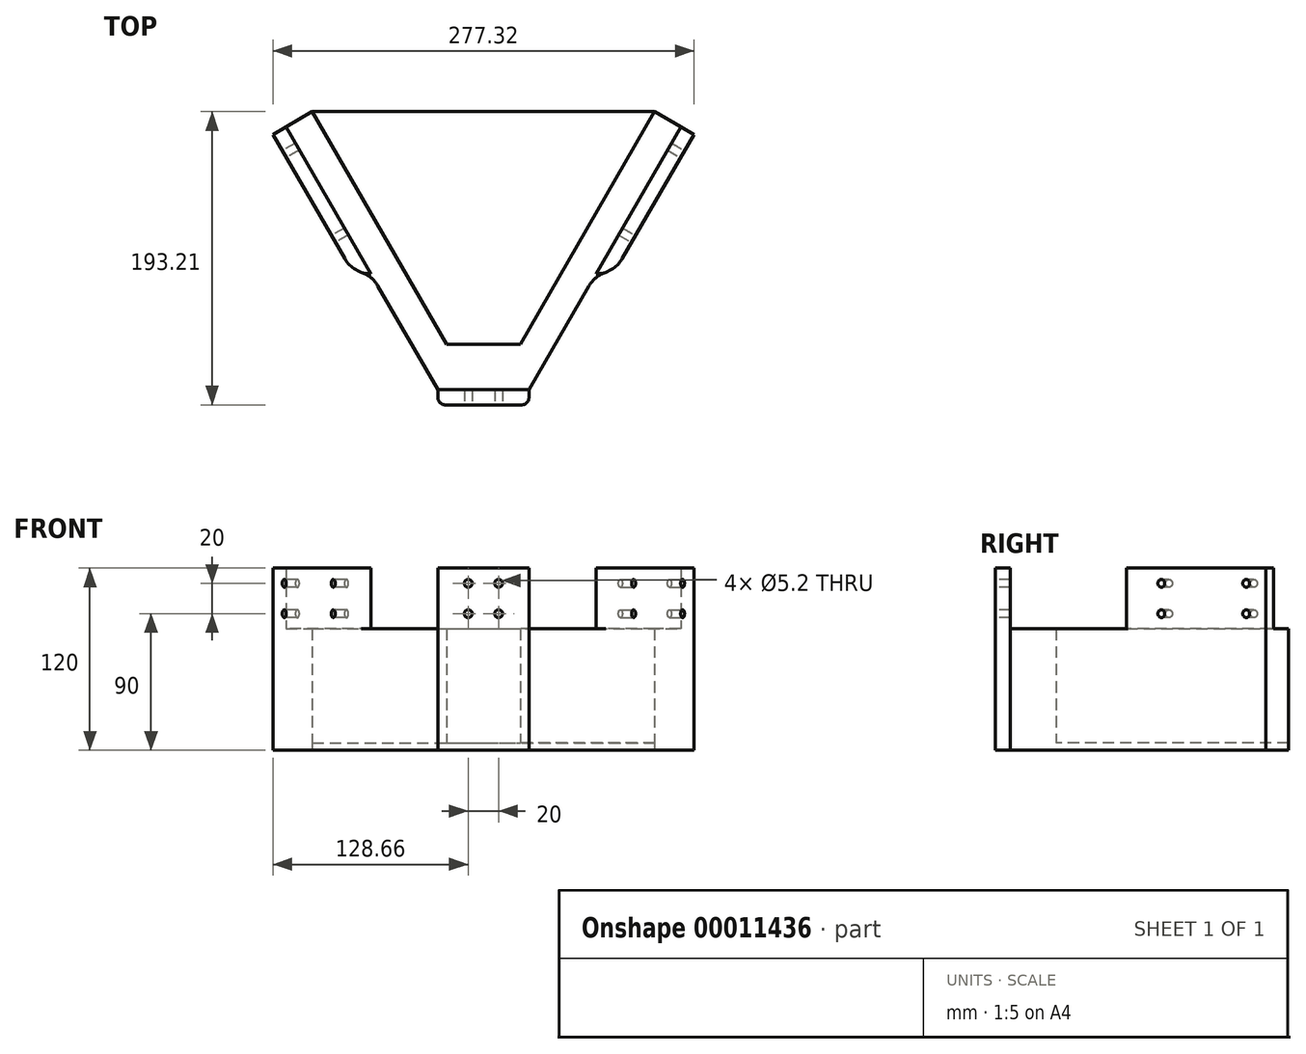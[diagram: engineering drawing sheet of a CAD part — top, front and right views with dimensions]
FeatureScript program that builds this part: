
annotation { "Feature Type Name" : "Feature", "Feature Type Description" : "" }
export const myFeature = defineFeature(function(context is Context, id is Id, definition is map)
    precondition{}
    {
        {
            var Q0;
            Q0=qCreatedBy(makeId("Top.planeOp"),FACE);
            var sketch = newSketch(context, id + "F0", { "sketchPlane" : qUnion([Q0])});
            skLineSegment(sketch, "E0.rect.bottom", {"start": v(-20, 20) * mm, "end": v(20, 20) * mm});
            skLineSegment(sketch, "E0.rect.top", {"start": v(-20, -20) * mm, "end": v(20, -20) * mm});
            skLineSegment(sketch, "E0.rect.left", {"start": v(-20, 20) * mm, "end": v(-20, -20) * mm});
            skLineSegment(sketch, "E0.rect.right", {"start": v(20, 20) * mm, "end": v(20, -20) * mm});
            skPoint(sketch, "E0.rect.middle", {"position": v(0, 0) * mm});
            skLineSegment(sketch, "E1.rect.bottom", {"start": v(-30, 30) * mm, "end": v(30, 30) * mm});
            skLineSegment(sketch, "E1.rect.top", {"start": v(-30, -30) * mm, "end": v(30, -30) * mm});
            skLineSegment(sketch, "E1.rect.left", {"start": v(-30, 30) * mm, "end": v(-30, -30) * mm});
            skLineSegment(sketch, "E1.rect.right", {"start": v(30, 30) * mm, "end": v(30, -30) * mm});
            skLineSegment(sketch, "E2", {"start": v(30, 30) * mm, "end": v(60, 81.96) * mm});
            skLineSegment(sketch, "E3", {"start": v(-30, 30) * mm, "end": v(-60, 81.96) * mm});
            skLineSegment(sketch, "E4", {"start": v(60, 81.96) * mm, "end": v(68.66, 76.96) * mm});
            skLineSegment(sketch, "E5", {"start": v(68.66, 76.96) * mm, "end": v(30, 10) * mm});
            skLineSegment(sketch, "E6", {"start": v(-60, 81.96) * mm, "end": v(-68.66, 76.96) * mm});
            skLineSegment(sketch, "E7", {"start": v(-68.66, 76.96) * mm, "end": v(-30, 10) * mm});
            skLineSegment(sketch, "E8", {"start": v(30, 30) * mm, "end": v(55.98, 15) * mm});
            skLineSegment(sketch, "E9", {"start": v(55.98, 15) * mm, "end": v(30, -30) * mm});
            skLineSegment(sketch, "E10", {"start": v(-30, 30) * mm, "end": v(-55.98, 15) * mm});
            skLineSegment(sketch, "E11", {"start": v(-55.98, 15) * mm, "end": v(-30, -30) * mm});
            skSolve(sketch);
        }
        {
            var Q0;
            Q0=qCreatedBy(makeId("Top.planeOp"),FACE);
            var sketch = newSketch(context, id + "F1", { "sketchPlane" : qUnion([Q0])});
            skPoint(sketch, "E12.rect.middle", {"position": v(0, 0) * mm});
            skLineSegment(sketch, "E13.rect.top", {"start": v(-30, -30) * mm, "end": v(30, -30) * mm});
            skLineSegment(sketch, "E14", {"start": v(30, -30) * mm, "end": v(130, 143.2) * mm});
            skLineSegment(sketch, "E15", {"start": v(130, 143.2) * mm, "end": v(138.66, 138.2) * mm});
            skLineSegment(sketch, "E16", {"start": v(138.66, 138.2) * mm, "end": v(41.55, -30) * mm});
            skLineSegment(sketch, "E17", {"start": v(41.55, -30) * mm, "end": v(30, -30) * mm});
            skLineSegment(sketch, "E18", {"start": v(-30, -30) * mm, "end": v(-130, 143.2) * mm});
            skLineSegment(sketch, "E19", {"start": v(-130, 143.2) * mm, "end": v(-138.66, 138.2) * mm});
            skLineSegment(sketch, "E20", {"start": v(-138.66, 138.2) * mm, "end": v(-41.55, -30) * mm});
            skLineSegment(sketch, "E21", {"start": v(-41.55, -30) * mm, "end": v(-30, -30) * mm});
            skLineSegment(sketch, "E22", {"start": v(-47.32, 0) * mm, "end": v(47.32, 0) * mm});
            skLineSegment(sketch, "E23", {"start": v(30, -30) * mm, "end": v(41.55, -30) * mm});
            skLineSegment(sketch, "E24", {"start": v(-130, 143.2) * mm, "end": v(-112.68, 153.2) * mm});
            skLineSegment(sketch, "E25", {"start": v(-112.68, 153.2) * mm, "end": v(-24.23, 0) * mm});
            skLineSegment(sketch, "E26", {"start": v(130, 143.2) * mm, "end": v(112.68, 153.2) * mm});
            skLineSegment(sketch, "E27", {"start": v(112.68, 153.2) * mm, "end": v(24.23, 0) * mm});
            skLineSegment(sketch, "E28", {"start": v(-47.32, 0) * mm, "end": v(-58.87, 0) * mm});
            skLineSegment(sketch, "E29", {"start": v(-58.87, 0) * mm, "end": v(58.87, 0) * mm});
            skLineSegment(sketch, "E30", {"start": v(-112.68, 153.2) * mm, "end": v(112.68, 153.2) * mm});
            skLineSegment(sketch, "E31", {"start": v(-85.6, 46.31) * mm, "end": v(-74.06, 46.31) * mm});
            skLineSegment(sketch, "E32", {"start": v(74.06, 46.31) * mm, "end": v(85.6, 46.31) * mm});
            skSolve(sketch);
        }
        {
            var Q0;
            {var subQ7=sQuery(id+"F1.wireOp",EDGE,"E13.rect.top");Q0=makeQuery(id+"F1.imprint","IMPRINT",FACE,{"disambiguationData":[TD([[makeQuery(id+"F1.imprint","IMPRINT",EDGE,{"derivedFrom":subQ7}),1.0]])]});}
            var Q1;
            {var subQ4=sQuery(id+"F1.wireOp",EDGE,"E24");Q1=makeQuery(id+"F1.imprint","IMPRINT",FACE,{"disambiguationData":[TD([[makeQuery(id+"F1.imprint","IMPRINT",EDGE,{"derivedFrom":subQ4}),-1.0]])]});}
            var Q2;
            {var subQ4=sQuery(id+"F1.wireOp",EDGE,"E26");Q2=makeQuery(id+"F1.imprint","IMPRINT",FACE,{"disambiguationData":[TD([[makeQuery(id+"F1.imprint","IMPRINT",EDGE,{"derivedFrom":subQ4}),1.0]])]});}
            extrude(context, id + "F2", {"entities" : qUnion([Q0, Q1, Q2]), "depth" : 80 * mm});
        }
        {
            var Q0;
            {var subQ2=sQuery(id+"F1.wireOp",EDGE,"E25");Q0=makeQuery(id+"F1.imprint","IMPRINT",FACE,{"disambiguationData":[TD([[makeQuery(id+"F1.imprint","IMPRINT",EDGE,{"derivedFrom":subQ2}),1.0]])]});}
            extrude(context, id + "F3", {"entities" : qUnion([Q0]), "operationType" : NewBodyOperationType.ADD, "depth" : 5 * mm});
        }
        {
            var Q0;
            {var subQ2=sQuery(id+"F1.wireOp",EDGE,"E19");Q0=makeQuery(id+"F1.imprint","IMPRINT",FACE,{"disambiguationData":[TD([[makeQuery(id+"F1.imprint","IMPRINT",EDGE,{"derivedFrom":subQ2}),1.0]])]});}
            var Q1;
            {var subQ2=sQuery(id+"F1.wireOp",EDGE,"E15");Q1=makeQuery(id+"F1.imprint","IMPRINT",FACE,{"disambiguationData":[TD([[makeQuery(id+"F1.imprint","IMPRINT",EDGE,{"derivedFrom":subQ2}),-1.0]])]});}
            extrude(context, id + "F4", {"entities" : qUnion([Q0, Q1]), "operationType" : NewBodyOperationType.ADD, "depth" : 120 * mm});
        }
        {
            var Q0;
            Q0=makeQuery(id+"F4.opExtrude","SWEPT_EDGE",EDGE,{"disambiguationData":[OSD([sQuery(id+"F1.wireOp",EDGE,"E20"),sQuery(id+"F1.wireOp",EDGE,"E31")])]});
            var Q1;
            Q1=makeQuery(id+"F4.opExtrude","SWEPT_EDGE",EDGE,{"disambiguationData":[OSD([sQuery(id+"F1.wireOp",EDGE,"E16"),sQuery(id+"F1.wireOp",EDGE,"E32")])]});
            fillet(context, id + "F5", {"entities" : qUnion([Q0, Q1]), "radius" : 20 * mm, "tangentPropagation" : true, "allowEdgeOverflow" : false});
        }
        {
            var Q0;
            Q0=makeQuery(id+"F5.opFillet","BLEND_EDGE",EDGE,{"blendedFrom":[makeQuery(id+"F4.opExtrude","SWEPT_EDGE",EDGE,{"disambiguationData":[OSD([sQuery(id+"F1.wireOp",EDGE,"E20"),sQuery(id+"F1.wireOp",EDGE,"E31")])]}),makeQuery(id+"F2.opExtrude","SWEPT_FACE",FACE,{"disambiguationData":[OSD([sQuery(id+"F1.wireOp",EDGE,"E18")])]})],"blendedInto":[makeQuery(id+"F2.opExtrude","SWEPT_FACE",FACE,{"disambiguationData":[OSD([sQuery(id+"F1.wireOp",EDGE,"E18")])]})]});
            var Q1;
            Q1=makeQuery(id+"F5.opFillet","BLEND_EDGE",EDGE,{"blendedFrom":[makeQuery(id+"F4.opExtrude","SWEPT_EDGE",EDGE,{"disambiguationData":[OSD([sQuery(id+"F1.wireOp",EDGE,"E16"),sQuery(id+"F1.wireOp",EDGE,"E32")])]}),makeQuery(id+"F2.opExtrude","SWEPT_FACE",FACE,{"disambiguationData":[OSD([sQuery(id+"F1.wireOp",EDGE,"E14")])]})],"blendedInto":[makeQuery(id+"F2.opExtrude","SWEPT_FACE",FACE,{"disambiguationData":[OSD([sQuery(id+"F1.wireOp",EDGE,"E14")])]})]});
            fillet(context, id + "F6", {"entities" : qUnion([Q0, Q1]), "radius" : 20 * mm, "tangentPropagation" : true, "allowEdgeOverflow" : false});
        }
        {
            var Q0;
            Q0=makeQuery(id+"F4.opExtrude","SWEPT_FACE",FACE,{"disambiguationData":[OSD([sQuery(id+"F1.wireOp",EDGE,"E20")])]});
            var sketch = newSketch(context, id + "F7", { "sketchPlane" : qUnion([Q0])});
            skCircle(sketch, "E33", {"center": v(-174.02, 110) * mm, "radius": 2.6 * mm});
            skCircle(sketch, "E34", {"center": v(-109.46, 110) * mm, "radius": 2.6 * mm});
            skCircle(sketch, "E35", {"center": v(-174.02, 90) * mm, "radius": 2.6 * mm});
            skCircle(sketch, "E36", {"center": v(-109.46, 90) * mm, "radius": 2.6 * mm});
            skSolve(sketch);
        }
        {
            var Q0;
            Q0 = qSketchRegion(id + "F7", true);
            extrude(context, id + "F8", {"entities" : qUnion([Q0]), "operationType" : NewBodyOperationType.REMOVE, "endBound" : BoundingType.THROUGH_ALL, "oppositeDirection" : true, "depth" : 25 * mm});
        }
        {
            var Q0;
            Q0=makeQuery(id+"F4.opExtrude","SWEPT_FACE",FACE,{"disambiguationData":[OSD([sQuery(id+"F1.wireOp",EDGE,"E16")])]});
            var sketch = newSketch(context, id + "F9", { "sketchPlane" : qUnion([Q0])});
            skCircle(sketch, "E37", {"center": v(109.46, 110) * mm, "radius": 2.6 * mm});
            skCircle(sketch, "E38", {"center": v(174.02, 110) * mm, "radius": 2.6 * mm});
            skCircle(sketch, "E39", {"center": v(109.46, 90) * mm, "radius": 2.6 * mm});
            skCircle(sketch, "E40", {"center": v(174.02, 90) * mm, "radius": 2.6 * mm});
            skSolve(sketch);
        }
        {
            var Q0;
            Q0 = qSketchRegion(id + "F9", true);
            extrude(context, id + "F10", {"entities" : qUnion([Q0]), "operationType" : NewBodyOperationType.REMOVE, "endBound" : BoundingType.THROUGH_ALL, "oppositeDirection" : true, "depth" : 25 * mm});
        }
        {
            var Q0;
            Q0=makeQuery(id+"F2.opExtrude","SWEPT_FACE",FACE,{"disambiguationData":[OSD([sQuery(id+"F1.wireOp",EDGE,"E13.rect.top")])]});
            var sketch = newSketch(context, id + "F11", { "sketchPlane" : qUnion([Q0])});
            skLineSegment(sketch, "E41.rect.bottom", {"start": v(-30, 120) * mm, "end": v(30, 120) * mm});
            skLineSegment(sketch, "E41.rect.top", {"start": v(-30, 0) * mm, "end": v(30, 0) * mm});
            skLineSegment(sketch, "E41.rect.left", {"start": v(-30, 120) * mm, "end": v(-30, 0) * mm});
            skLineSegment(sketch, "E41.rect.right", {"start": v(30, 120) * mm, "end": v(30, 0) * mm});
            skPoint(sketch, "E41.rect.middle", {"position": v(0, 60) * mm});
            skSolve(sketch);
        }
        {
            var Q0;
            Q0 = qSketchRegion(id + "F11", true);
            extrude(context, id + "F12", {"entities" : qUnion([Q0]), "operationType" : NewBodyOperationType.ADD, "depth" : 10 * mm});
        }
        {
            var Q0;
            Q0=makeQuery(id+"F12.opExtrude","CAP_FACE",FACE,{"disambiguationData":[OSD([sQuery(id+"F11.wireOp",EDGE,"E41.rect.bottom"),sQuery(id+"F11.wireOp",EDGE,"E41.rect.top"),sQuery(id+"F11.wireOp",EDGE,"E41.rect.left"),sQuery(id+"F11.wireOp",EDGE,"E41.rect.right")])],"isStart":false});
            var sketch = newSketch(context, id + "F13", { "sketchPlane" : qUnion([Q0])});
            skCircle(sketch, "E42", {"center": v(-10, 110) * mm, "radius": 2.6 * mm});
            skCircle(sketch, "E43", {"center": v(-10, 90) * mm, "radius": 2.6 * mm});
            skCircle(sketch, "E44", {"center": v(10, 110) * mm, "radius": 2.6 * mm});
            skCircle(sketch, "E45", {"center": v(10, 90) * mm, "radius": 2.6 * mm});
            skSolve(sketch);
        }
        {
            var Q0;
            Q0 = qSketchRegion(id + "F13", true);
            extrude(context, id + "F14", {"entities" : qUnion([Q0]), "operationType" : NewBodyOperationType.REMOVE, "endBound" : BoundingType.THROUGH_ALL, "oppositeDirection" : true, "depth" : 25 * mm});
        }
        {
            var Q0;
            Q0=makeQuery(id+"F12.opExtrude","CAP_EDGE",EDGE,{"disambiguationData":[OSD([sQuery(id+"F11.wireOp",EDGE,"E41.rect.left")])],"isStart":false});
            var Q1;
            Q1=makeQuery(id+"F12.opExtrude","CAP_EDGE",EDGE,{"disambiguationData":[OSD([sQuery(id+"F11.wireOp",EDGE,"E41.rect.right")])],"isStart":false});
            fillet(context, id + "F15", {"entities" : qUnion([Q0, Q1]), "radius" : 5 * mm, "tangentPropagation" : true, "allowEdgeOverflow" : false});
        }
    });
